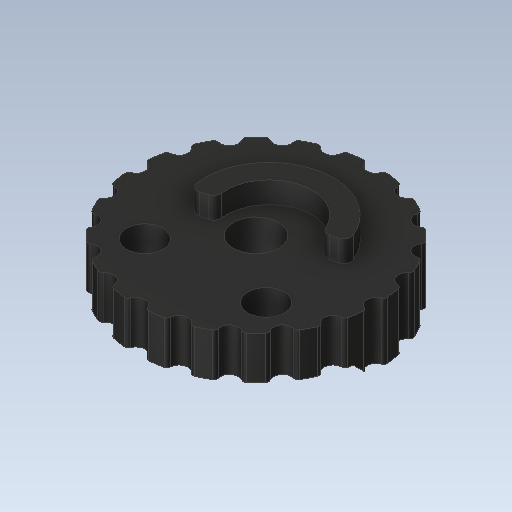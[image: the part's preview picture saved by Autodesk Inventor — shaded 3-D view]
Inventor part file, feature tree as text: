
AUTODESK INVENTOR PART (.ipt)
format: ipt  version: 2020.1 (Build 241239000, 239)  size: 359,936 bytes
history: native  units: mm
features: extrude x6, sketch x2, fillet x1, draft x1
ambient origin geometry x8: Origin, YZ Plane, XZ Plane, XY Plane, X Axis, Y Axis, Z Axis, Center Point
bodies: Solid1 (feature_tree)
feature tree (10):
  extrude  "Extrusion1"  Depth=1.25mm
  fillet  "Fillet1"  Radius=8.0mm
  sketch  "Sketch2"  dims[d10=6.3mm d11=12.0mm d12=7.0mm d14=2.0mm d15=0.0mm d16=2.0mm d17=0.0mm d18=0.5mm d19=1.745329mm d20=45.0deg d22=5.1mm d23=5.1mm d25=8.726646mm d26=1.5mm d27=9.0mm d28=6.0mm d29=7.330383mm d30=11.5mm d31=11.0mm d32=1.0mm d33=1.5mm d34=1.5mm d35=3.0mm d36=0.0mm d37=5.0mm d38=0.0mm d39=5.0mm d40=0.0mm d41=9.599311mm d43=180.0deg d44=0.0mm]
  extrude  "Extrusion2"  Depth=5.0mm
  extrude  "Extrusion3"  Depth=5.0mm
  draft  "FaceDraft1"
  extrude  "Extrusion4"  Depth=2.0mm TaperAngle=0.0deg
  extrude  "Extrusion5"  Depth=2.0mm TaperAngle=0.0deg
  extrude  "Extrusion6"  Depth=0.5mm
  sketch  "Sketch1"  dims[d1=200.0mm d2=31.0mm d3=360.0deg d6=1.25mm d7=1.25mm d8=8.0mm d9=0.0mm]
